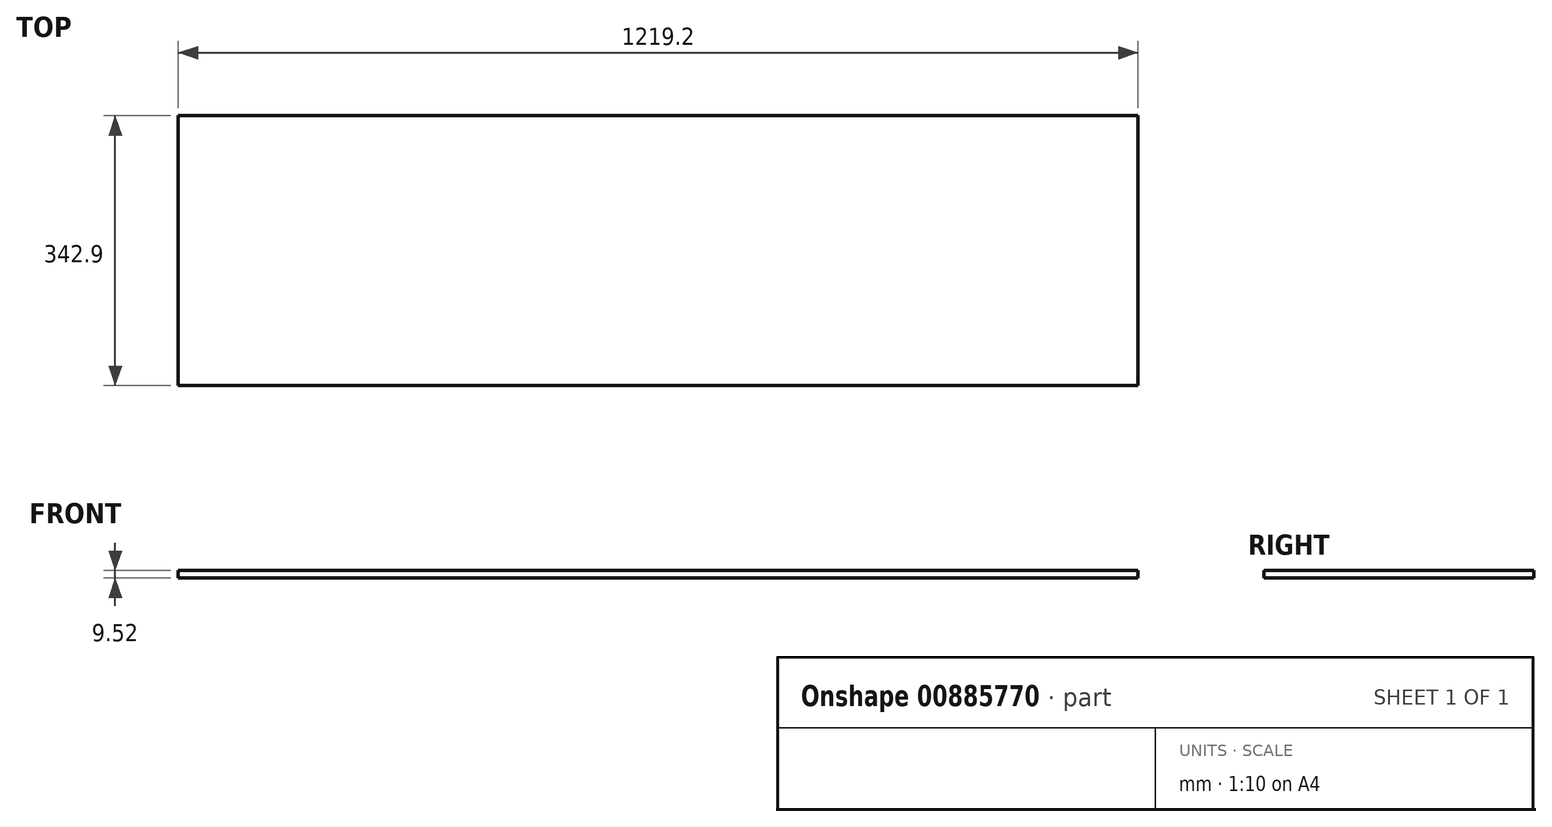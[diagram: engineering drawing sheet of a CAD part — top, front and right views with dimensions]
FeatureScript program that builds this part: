
annotation { "Feature Type Name" : "Feature", "Feature Type Description" : "" }
export const myFeature = defineFeature(function(context is Context, id is Id, definition is map)
    precondition{}
    {
        {
            var Q0;
            Q0=qCreatedBy(makeId("Top.planeOp"),FACE);
            var sketch = newSketch(context, id + "F0", { "sketchPlane" : qUnion([Q0])});
            skLineSegment(sketch, "E0.bottom", {"start": v(609.6, -171.45) * mm, "end": v(-609.6, -171.45) * mm});
            skLineSegment(sketch, "E0.top", {"start": v(609.6, 171.45) * mm, "end": v(-609.6, 171.45) * mm});
            skLineSegment(sketch, "E0.left", {"start": v(609.6, -171.45) * mm, "end": v(609.6, 171.45) * mm});
            skLineSegment(sketch, "E0.right", {"start": v(-609.6, -171.45) * mm, "end": v(-609.6, 171.45) * mm});
            skPoint(sketch, "E0.middle", {"position": v(0, 0) * mm});
            skSolve(sketch);
        }
        {
            var Q0;
            Q0=makeQuery(id+"F0.imprint","IMPRINT",FACE,{"disambiguationData":[TD([[makeQuery(id+"F0.imprint","IMPRINT",EDGE,{"derivedFrom":sQuery(id+"F0.wireOp",EDGE,"E0.bottom")}),-1.0]])]});
            extrude(context, id + "F1", {"entities" : qUnion([Q0]), "endBound" : BoundingType.SYMMETRIC, "depth" : 9.52 * mm, "offsetDistance" : 25.4 * mm});
        }
    });
